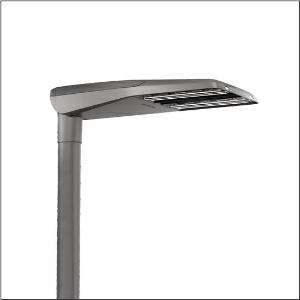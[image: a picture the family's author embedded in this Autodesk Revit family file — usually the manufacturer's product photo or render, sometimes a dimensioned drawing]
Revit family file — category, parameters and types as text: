
# Revit family: streetlight_sl_11_iq_midi___st1_2a_5xc3a21f08me_5047
name_source: partatom
category: Lighting Fixtures
units: mm (PartAtom-declared; Revit-internal decimal feet)

## family parameters
Cut with Voids When Loaded = No
Host = Face
Light Source = No
Part Type = Normal
Room Calculation Point = No
Round Connector Dimension = Use Diameter
Shared = No

## types (1)
- --- (1 x LED, 14840 lm, 124.7 W, 2200K)
    Apparent Load = 125 VA
    CIE Flux Codes = 32 70 96 100 100
    Color Rendering = 70
    Color Temperature = 2200K
    Default Elevation = 1800 mm
    Description = Streetlight SL 11 iQ midi, mast luminaire, primary light control with 3 zone facetted reflector, of plastic, silver coated, highly specular, primary optical cover: cover, of PMMA, transparent, light distribution: ST1.2a, light emission: direct distribution, primary light characteristic: asymmetric, installation type: post-top, side-entry, LED, High Power LED, rated luminous flux: 14.840lm, luminous efficacy: 119lm/W, light colour: 722, colour temperature: 2200K, control: Street-Remote, optimised constant luminous flux control (CLO 2.0), Desk-Remote (wireless, voltage-free reading and setting of iQ features in the workshop via application-optimized NFC function/RFID function), Light-Fading, Smart-Wire, Night-Set, Lumen-Switch, Temp-Guard, Auto-Match, with cable H07RN-F 5x 1.5mm², mains connection: 230..240V, AC, 50/60Hz, connection cable pre-assembled, cable length: 12,5m, start of lifetime: 125W, end of service life: 132W, reduction: 57W, luminaire housing, of diecast aluminium, powder-coated, Siteco® metallic grey (DB 702S), please order mast flange separately, inclination adjustable without tools: 0°, 5°, 10°, 15° (post-top) | 0°, -5°, -10°, -15° (side-entry), sealing non-destructively replaceable, multi-level sealing system, length: 780mm, width: 376mm, height: 118mm, mast flange for spigot size: 42mm (side-entry): 5XC10008XM4, 60/48mm (side-entry/post-top): 5XC10108XM2, 76/60mm (side-entry/post-top): 5XC10108XM1, equipment: Power, protection rating (complete): IP66, insulation class (complete): insulation class II (safety insulation), certification: CE, ENEC, VDE, impact resistance: IK09, permissible operating ambient temperature for outdoor applications: -25..+50°C, standard-compliant lighting for roads and squares, Environmental Product Declaration (EPD) tested and certified by an independent institute, packaging unit: 1 piece

Light Distribution: ST1.2a
    Height = 118 mm
    Lamp = 1 x LED
    Lamp Light Flux = 14840 lm
    Lamp Power = 124.7 W
    Lamp count = 1
    Length = 780 mm
    Luminous efficacy = 119 lm/W
    Manufacturer = Siteco
    ModVariant = No
    Model = 5XC3A21F08ME
    Number of Poles = 1
    OnlyDefault = Yes
    Power Factor = 1
    Product Name = Streetlight SL 11 iQ midi | ST1.2a
    Product group = mast luminaire | pylon top
    ProductGroupID = 6100
    Protection Class = Protection class II
    Protection Degree = IP 66
    RLX_Detail_Level = 1
    RLX_Emergency_Light_Flux = 0 lm
    RLX_Emergency_Type = 0
    RLX_Emergency_Type_DB = No
    RlxData = <blob elided: 70709 chars, md5=97fb0a81>
    Socket = socket
    Standby Power = 0 W
    System Light Flux = 14841 lm
    System Power = 125 W
    Type Comments = factory setting: luminous flux: 100 % | dim-lin: 254 | 557 mA
    Type Image = l_1005960.jpg
    URL = http://relux.com
    VarID = @adj_061077
    Voltage = 0 V
    Weight = 0.00 kg
    Width = 376 mm

## geometry (parser evidence)
native form markers: Blend x4, Sweep x8
no freeform markers — native parametric forms only
